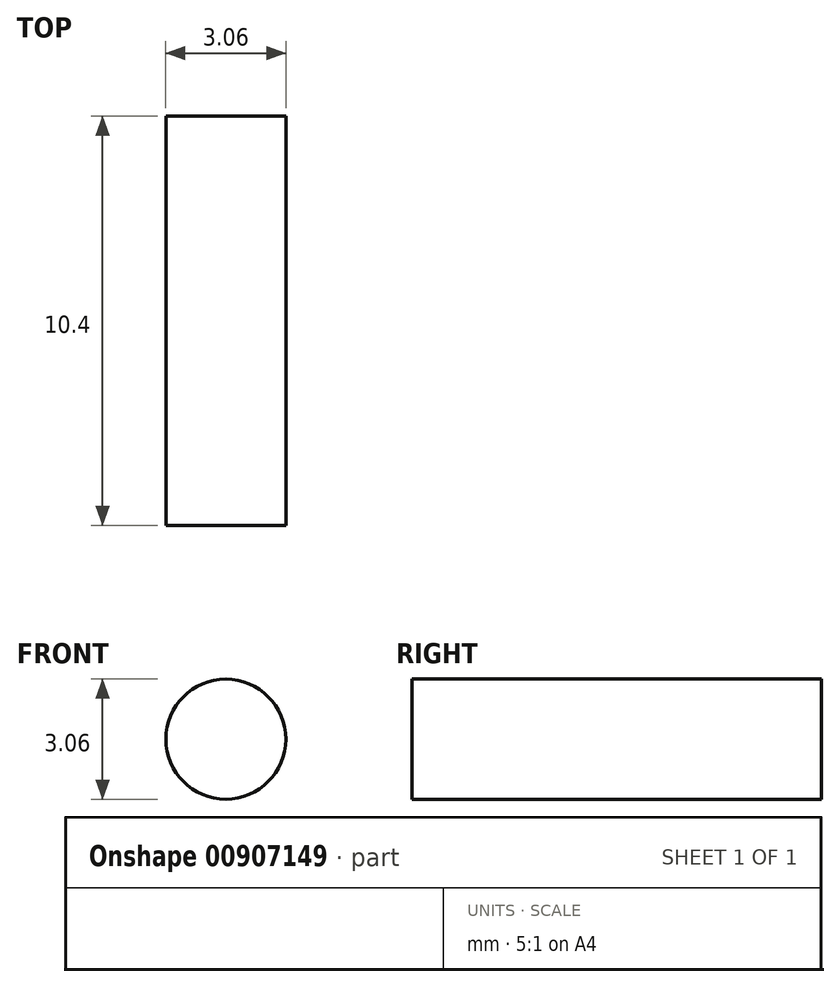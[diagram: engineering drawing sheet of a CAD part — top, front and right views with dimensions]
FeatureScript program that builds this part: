
annotation { "Feature Type Name" : "Feature", "Feature Type Description" : "" }
export const myFeature = defineFeature(function(context is Context, id is Id, definition is map)
    precondition{}
    {
        {
            var Q0;
            Q0=qCreatedBy(makeId("Front.planeOp"),FACE);
            var sketch = newSketch(context, id + "F0", { "sketchPlane" : qUnion([Q0])});
            skCircle(sketch, "E0", {"center": v(0, 0) * mm, "radius": 1.53 * mm});
            skSolve(sketch);
        }
        {
            var Q0;
            Q0 = qSketchRegion(id + "F0", true);
            extrude(context, id + "F1", {"entities" : qUnion([Q0]), "depth" : 10.4 * mm, "offsetDistance" : 25 * mm});
        }
    });
